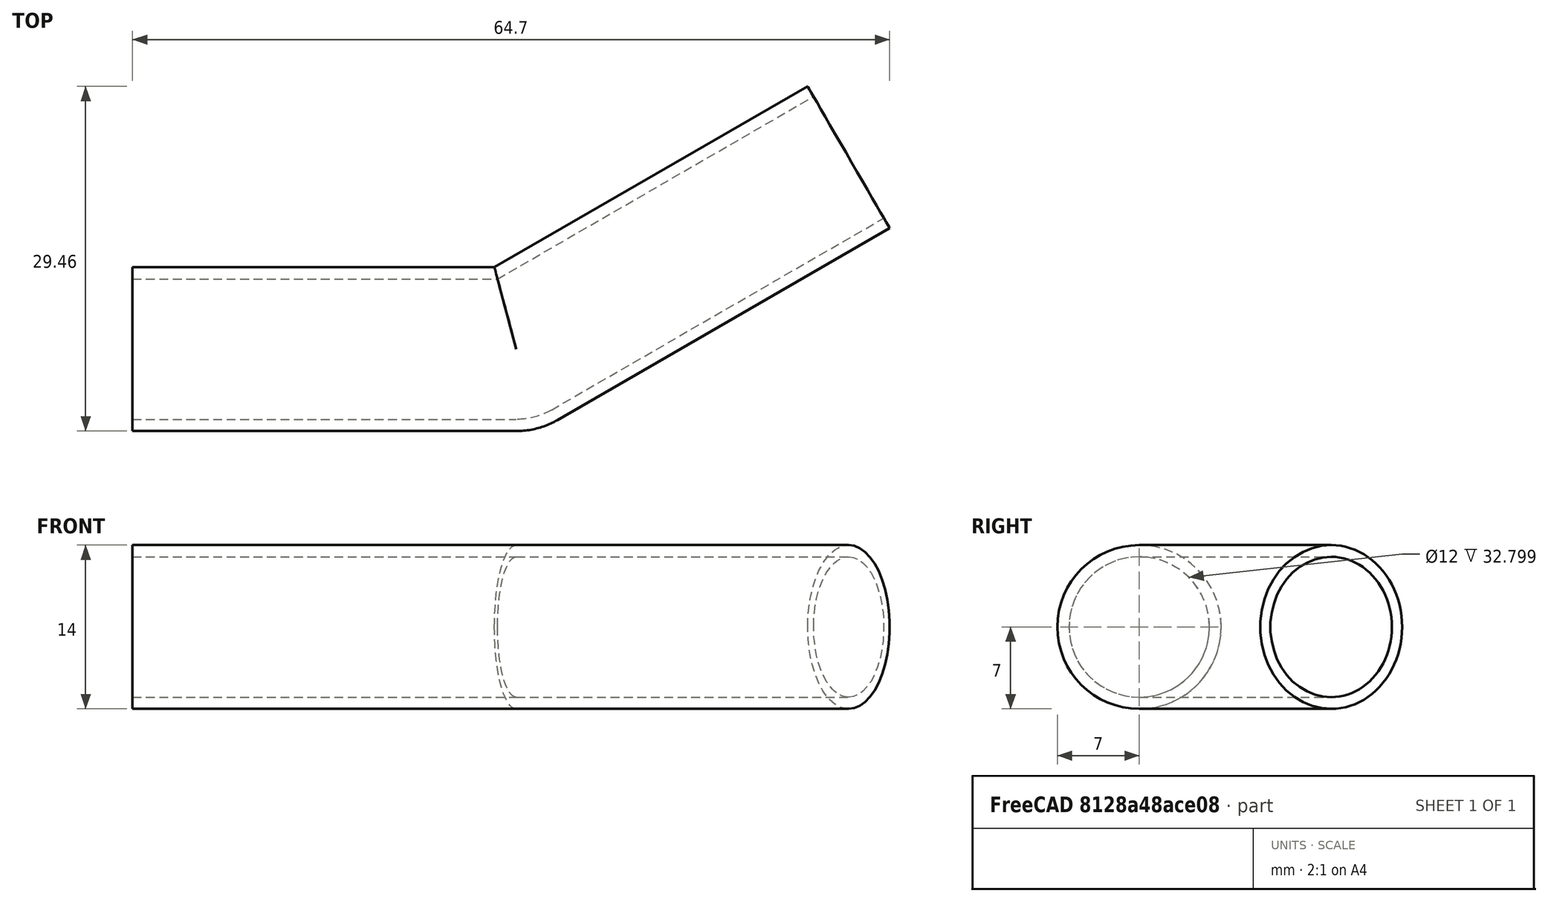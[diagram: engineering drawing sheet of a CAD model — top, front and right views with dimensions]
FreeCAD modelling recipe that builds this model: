
FCSTD DOCUMENT  (FreeCAD 0.21R33694 (Git))
Label: awning_channel_tunnel
License: All rights reserved
LicenseURL: https://en.wikipedia.org/wiki/All_rights_reserved
objects: Sketcher::SketchObject×2, PartDesign::AdditivePipe×1, PartDesign::Body×1
note: 5 computed .brp shape members not serialized (recipe doc carries the construction recipe); baked Part::Feature solids carry a one-line shape summary decoded from their .brp

FEATURE [Sketcher::SketchObject] Sketch
  FullyConstrained = false
  MapMode = 5
  Support = -> [XY_Plane]
  expr: Constraints[4] = 180 ° - 30 °
  sketch-geometry (2):
    g0: LineSegment StartX=0 StartY=0 StartZ=0 EndX=32.7992 EndY=0 EndZ=0
    g1: LineSegment StartX=61.2042 StartY=16.3996 StartZ=0 EndX=32.7992 EndY=0 EndZ=0
  constraints (5):
    c: Coincident(g0,g-1)
    c: PointOnObject(g0,g-1)
    c: Coincident(g1,g0)
    c: Equal(g0,g1)
    c: Angle(g1,g0) = 2.61799
FEATURE [Sketcher::SketchObject] Sketch001
  FullyConstrained = true
  MapMode = 5
  Placement = pos=(0,0,0) rot=(0.57735,0.57735,0.57735;2.0944rad)
  Support = -> [YZ_Plane]
  sketch-geometry (2):
    g0: Circle CenterX=0 CenterY=0 CenterZ=0 NormalX=0 NormalY=0 NormalZ=1 AngleXU=0 Radius=7
    g1: Circle CenterX=0 CenterY=0 CenterZ=0 NormalX=0 NormalY=0 NormalZ=1 AngleXU=0 Radius=6
  constraints (4):
    c: Coincident(g0,g-1)
    c: Diameter(g0) = 14
    c: Coincident(g1,g0)
    c: Diameter(g1) = 12
FEATURE [PartDesign::AdditivePipe] AdditivePipe
  AuxilleryCurvelinear = true
  AuxillerySpineTangent = false
  Binormal = (0,0,0)
  Mode = 2
  Placement = pos=(0,0,0) rot=(1,1,1;2.0944rad)
  Profile = -> Sketch001
  Spine = -> Sketch
  SpineTangent = false
  Transformation = 0
  Transition = 2
FEATURE [PartDesign::Body] Body
  Group = -> [Sketch,Sketch001,AdditivePipe]
  Origin = -> Origin
  Tip = -> AdditivePipe
